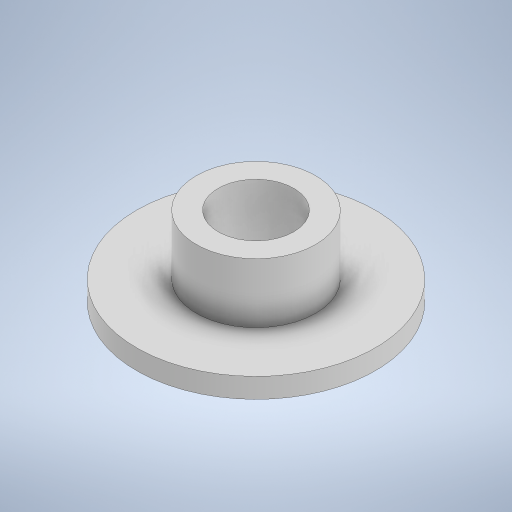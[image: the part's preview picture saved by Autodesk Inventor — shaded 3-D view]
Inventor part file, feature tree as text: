
AUTODESK INVENTOR PART (.ipt)
format: ipt  version: 2024.1 (Build 281209000, 209)  size: 240,128 bytes
history: native  units: mm
features: extrude x3, sketch x3, other x1
ambient origin geometry x8: Origin, YZ Plane, XZ Plane, XY Plane, X Axis, Y Axis, Z Axis, Center Point
bodies: Body1 (feature_tree)
feature tree (7):
  other  "ソリッド1"
  extrude  "押し出し1"  Depth=12.0mm
  extrude  "押し出し2"  Depth=1.0mm TaperAngle=0.0deg
  extrude  "押し出し3"  Depth=6.0mm
  sketch  "スケッチ1"
  sketch  "スケッチ2"
  sketch  "スケッチ3"
